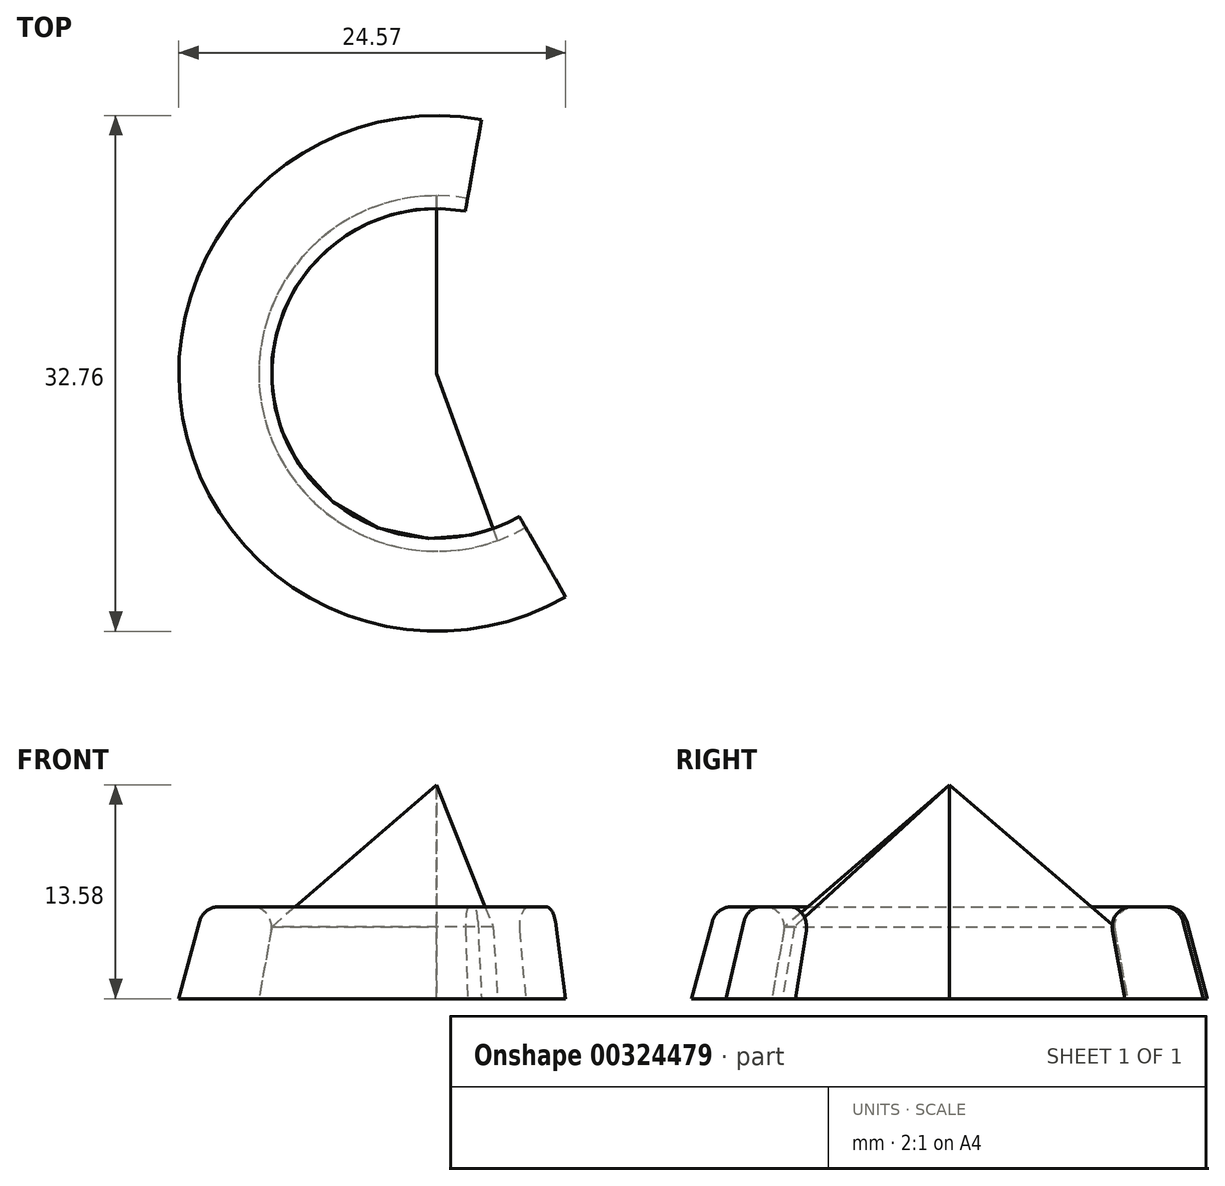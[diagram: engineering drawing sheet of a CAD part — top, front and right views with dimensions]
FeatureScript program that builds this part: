
annotation { "Feature Type Name" : "Feature", "Feature Type Description" : "" }
export const myFeature = defineFeature(function(context is Context, id is Id, definition is map)
    precondition{}
    {
        {
            var Q0;
            Q0=qCreatedBy(makeId("Right.planeOp"),FACE);
            var sketch = newSketch(context, id + "F0", { "sketchPlane" : qUnion([Q0])});
            skLineSegment(sketch, "E0", {"start": v(0, 0) * mm, "end": v(0, 13.58) * mm});
            skLineSegment(sketch, "E1", {"start": v(10.24, 5.84) * mm, "end": v(11.3, 0) * mm});
            skLineSegment(sketch, "E2", {"start": v(11.3, 0) * mm, "end": v(0, 0) * mm});
            skLineSegment(sketch, "E3", {"start": v(10.24, 5.84) * mm, "end": v(14.81, 5.84) * mm});
            skLineSegment(sketch, "E4", {"start": v(14.81, 5.84) * mm, "end": v(16.38, 0) * mm});
            skLineSegment(sketch, "E5", {"start": v(16.38, 0) * mm, "end": v(11.3, 0) * mm});
            skLineSegment(sketch, "E6", {"start": v(0, 13.58) * mm, "end": v(10.47, 4.57) * mm});
            skSolve(sketch);
        }
        {
            var Q0;
            Q0=makeQuery(id+"F0.imprint","IMPRINT",FACE,{"disambiguationData":[TD([[makeQuery(id+"F0.imprint","IMPRINT",EDGE,{"derivedFrom":sQuery(id+"F0.wireOp",EDGE,"E0")}),-1.0]])]});
            var Q1;
            Q1=sQuery(id+"F0.wireOp",EDGE,"E0");
            revolve(context, id + "F1", {"entities" : qUnion([Q0]), "axis" : qUnion([Q1]), "revolveType" : RevolveType.ONE_DIRECTION, "angle" : 200 * degree});
        }
        {
            var Q0;
            Q0=makeQuery(id+"F0.imprint","IMPRINT",FACE,{"disambiguationData":[TD([[makeQuery(id+"F0.imprint","IMPRINT",EDGE,{"derivedFrom":sQuery(id+"F0.wireOp",EDGE,"E1")}),1.0]])]});
            var Q1;
            Q1=sQuery(id+"F0.wireOp",EDGE,"E0");
            revolve(context, id + "F2", {"entities" : qUnion([Q0]), "axis" : qUnion([Q1]), "revolveType" : RevolveType.TWO_DIRECTIONS, "angle" : 210 * degree, "angleBack" : 350 * degree});
        }
        {
            var Q0;
            Q0=makeQuery(id+"F2.opRevolve","SWEPT_EDGE",EDGE,{"disambiguationData":[OSD([sQuery(id+"F0.wireOp",EDGE,"E1"),sQuery(id+"F0.wireOp",EDGE,"E3")])]});
            var Q1;
            Q1=makeQuery(id+"F2.opRevolve","SWEPT_EDGE",EDGE,{"disambiguationData":[OSD([sQuery(id+"F0.wireOp",EDGE,"E3"),sQuery(id+"F0.wireOp",EDGE,"E4")])]});
            fillet(context, id + "F3", {"entities" : qUnion([Q0, Q1]), "radius" : 1.27 * mm, "tangentPropagation" : true, "allowEdgeOverflow" : false});
        }
    });
